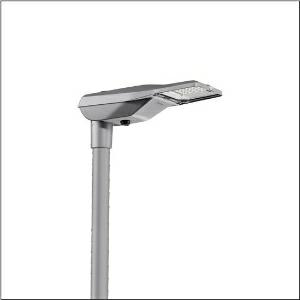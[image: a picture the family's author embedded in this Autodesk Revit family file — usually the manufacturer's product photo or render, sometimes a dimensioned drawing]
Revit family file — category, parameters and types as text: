
# Revit family: streetlight_sl_21_micro___p0_5a_5xe1v33r08db_e47d
name_source: partatom
category: Lighting Fixtures
units: mm (PartAtom-declared; Revit-internal decimal feet)

## family parameters
Cut with Voids When Loaded = No
Host = Face
Light Source = No
Part Type = Normal
Room Calculation Point = No
Round Connector Dimension = Use Diameter
Shared = No

## types (1)
- --- (1 x LED, 4940 lm, 39.1 W, 3000K)
    Apparent Load = 39 VA
    CIE Flux Codes = 37 73 96 100 100
    Color Rendering = 70
    Color Temperature = 3000K
    Default Elevation = 1800 mm
    Description = Streetlight SL 21 micro, mast luminaire, primary light control with lens, of PMMA, primary optical cover: cover, of toughened safety glass, transparent, light distribution: P0.5a, light emission: direct distribution, primary light characteristic: asymmetric, installation type: post-top, side-entry, LED, High Power LED, rated luminous flux: 4.940lm, luminous efficacy: 126lm/W, light colour: 730, colour temperature: 3000K, control gear: D4i, control: pre-setting: logarithmic dimming characteristic, flexible luminous flux parameterisation, time-dependent luminous flux control, constant luminous flux control, overheat protection, mains connection: 220..240V, AC, 50/60Hz, start of lifetime: 39W, end of service life: 41W, reduction: 18W, luminaire housing, of diecast aluminium, powder-coated, Siteco® metallic grey (DB 702S), corrosivity category C5 mid according to DIN EN ISO 12944, multi-level sealing system, sealing non-destructively replaceable, inclination adjustable: 0°, 5°, 10°, 15°, please order mast flange separately, length: 528mm, width: 235mm, height: 110mm, mast flange for spigot size: 42mm (side-entry): 5XC10008XM4, 60/48mm (side-entry/post-top): 5XC10108XM2, 76/60mm (side-entry/post-top): 5XC10108XM1, Smart Interface below, protection rating (complete): IP66, insulation class (complete): insulation class II (safety insulation), certification: CE, ENEC, ENEC+, VDE, impact resistance: IK10, permissible operating ambient temperature for outdoor applications: -40..+50°C, standard-compliant lighting for roads and squares, packaging unit: 1 piece

Light Distribution: P0.5a
    Height = 110 mm
    Lamp = 1 x LED
    Lamp Light Flux = 4940 lm
    Lamp Power = 39.1 W
    Lamp count = 1
    Length = 528 mm
    Luminous efficacy = 126 lm/W
    Manufacturer = Siteco
    ModVariant = No
    Model = 5XE1V33R08DB
    Number of Poles = 1
    OnlyDefault = Yes
    Power Factor = 1
    Product Name = Streetlight SL 21 micro | P0.5a
    Product group = mast luminaire | pylon top
    ProductGroupID = 6100
    Protection Class = Protection class II
    Protection Degree = IP 66
    RLX_Detail_Level = 1
    RLX_Emergency_Light_Flux = 0 lm
    RLX_Emergency_Type = 0
    RLX_Emergency_Type_DB = No
    RlxData = <blob elided: 98361 chars, md5=69c6aa38>
    Socket = socket
    Standby Power = 0 W
    System Light Flux = 4940 lm
    System Power = 39 W
    Type Comments = factory setting: luminous flux: 100 % | dim-lin: 254 | 765 mA
    Type Image = l_1277290.jpg
    URL = http://relux.com
    VarID = @adj_091665
    Voltage = 0 V
    Weight = 0.00 kg
    Width = 235 mm

## geometry (parser evidence)
native form markers: Blend x4, Sweep x9
no freeform markers — native parametric forms only
